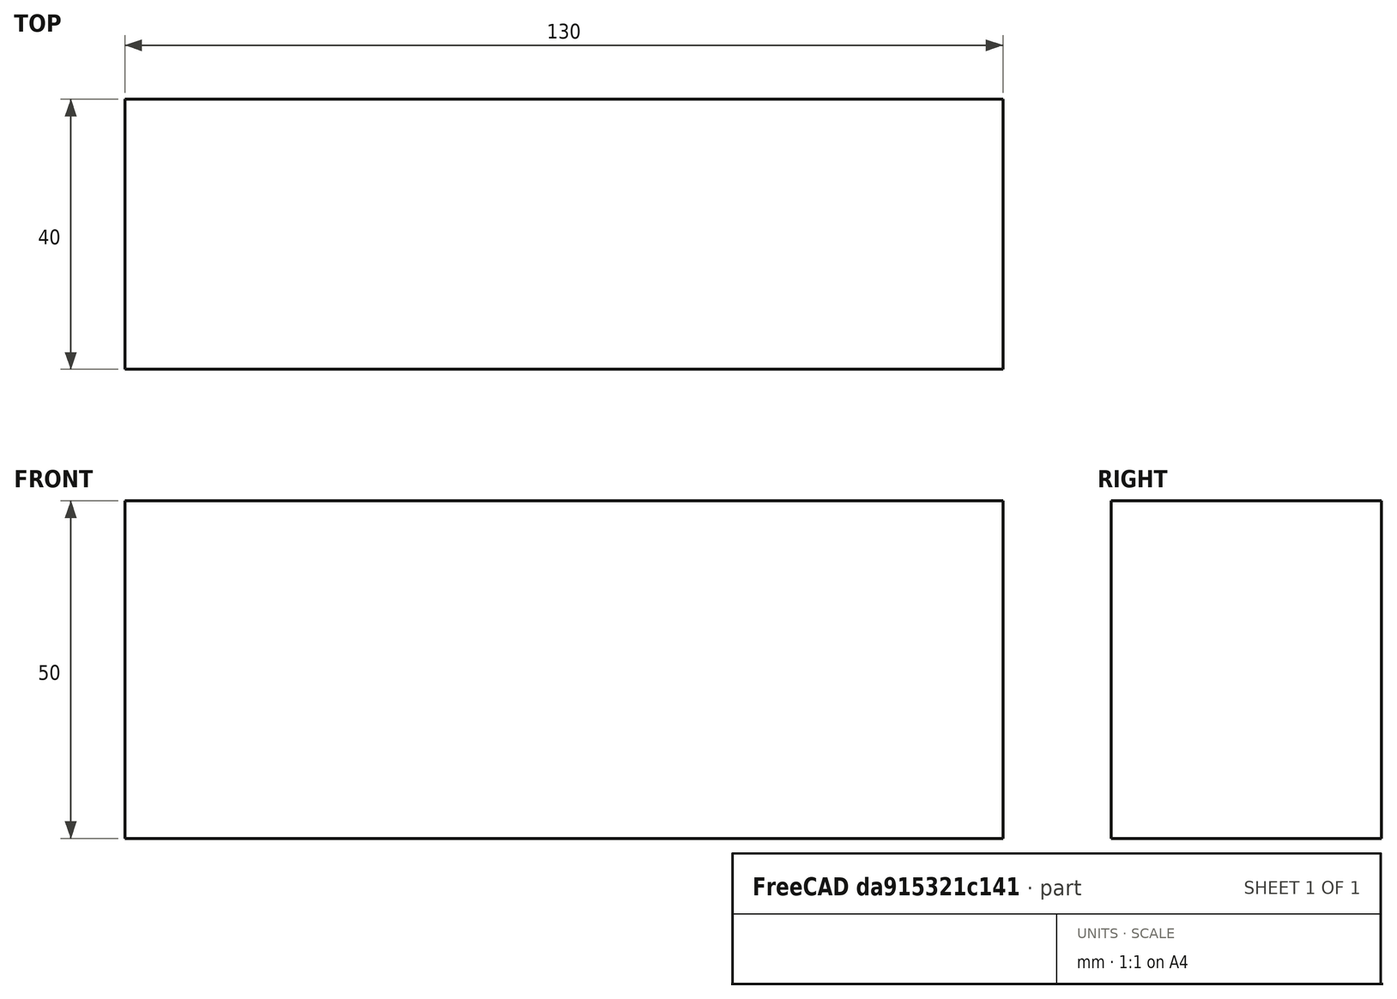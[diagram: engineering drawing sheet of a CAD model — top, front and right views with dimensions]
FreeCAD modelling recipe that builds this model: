
FCSTD DOCUMENT  (FreeCAD 0.15R4671 (Git))
Label: Flat Bar 130x40 EN10058 S235JR
License: All rights reserved
LicenseURL: http://en.wikipedia.org/wiki/All_rights_reserved
objects: Sketcher::SketchObject×1, Part::Extrusion×1
note: 2 computed .brp shape members not serialized (recipe doc carries the construction recipe); baked Part::Feature solids carry a one-line shape summary decoded from their .brp

FEATURE [Sketcher::SketchObject] Sketch
  sketch-geometry (4):
    g0: LineSegment StartX=-65 StartY=-20 StartZ=0 EndX=65 EndY=-20 EndZ=0
    g1: LineSegment StartX=65 StartY=-20 StartZ=0 EndX=65 EndY=20 EndZ=0
    g2: LineSegment StartX=65 StartY=20 StartZ=0 EndX=-65 EndY=20 EndZ=0
    g3: LineSegment StartX=-65 StartY=20 StartZ=0 EndX=-65 EndY=-20 EndZ=0
  constraints (12):
    c: Coincident(g0,g1)
    c: Coincident(g1,g2)
    c: Coincident(g2,g3)
    c: Coincident(g3,g0)
    c: Horizontal(g0)
    c: Horizontal(g2)
    c: Vertical(g1)
    c: Vertical(g3)
    c: Symmetric(g1,g2,g-2)
    c: Symmetric(g0,g1,g-1)
    c: DistanceY(g1) = 40
    c: DistanceX(g0) = 130
FEATURE [Part::Extrusion] Extrude  label="Flat Bar 130x40 EN10058 S235JR"
  Base = -> Sketch
  Dir = (0,0,50)
  Solid = true
